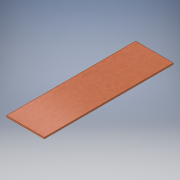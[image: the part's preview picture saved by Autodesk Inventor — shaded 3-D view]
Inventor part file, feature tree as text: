
AUTODESK INVENTOR PART (.ipt)
format: ipt  version: 2018 (Build 220112000, 112)  size: 100,352 bytes
history: native  units: mm
features: extrude x1, sketch x1
ambient origin geometry x8: Origin, YZ Plane, XZ Plane, XY Plane, X Axis, Y Axis, Z Axis, Center Point
bodies: Volumenkörper1 (feature_tree)
feature tree (2):
  extrude  "Extrusion1"  Depth=109.5mm
  sketch  "Skizze1"  dims[d0=32.0mm d1=109.5mm d2=1.2mm d3=0.0mm]
